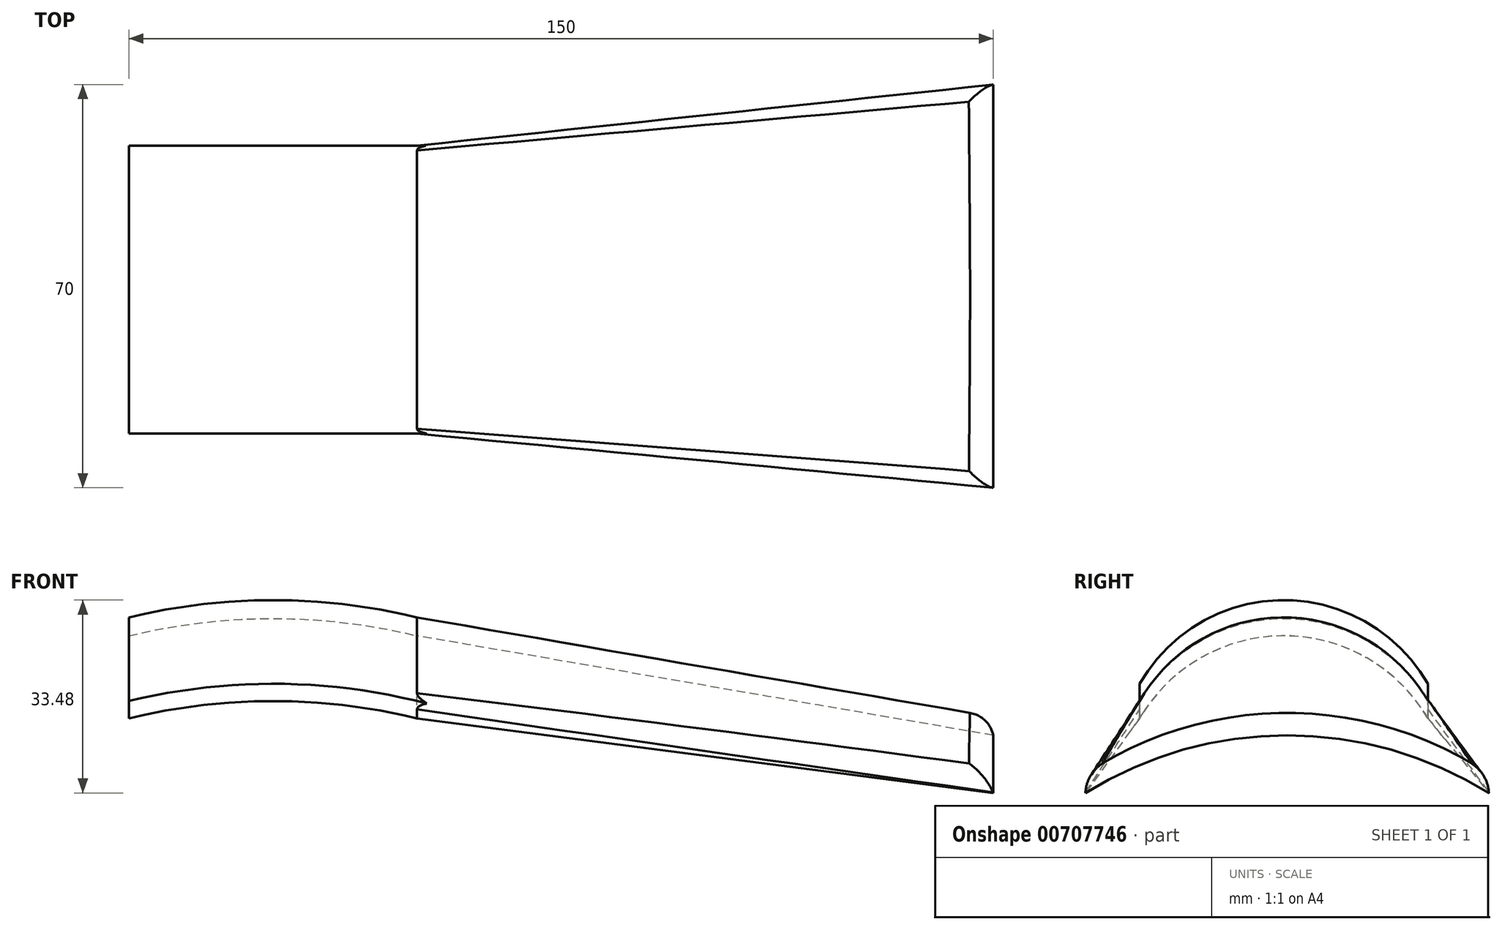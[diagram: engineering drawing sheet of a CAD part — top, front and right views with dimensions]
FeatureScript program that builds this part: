
annotation { "Feature Type Name" : "Feature", "Feature Type Description" : "" }
export const myFeature = defineFeature(function(context is Context, id is Id, definition is map)
    precondition{}
    {
        {
            var Q0;
            Q0=qCreatedBy(makeId("Right.planeOp"),FACE);
            var sketch = newSketch(context, id + "F0", { "sketchPlane" : qUnion([Q0])});
            skArc(sketch, "E0", {"start": v(50, 0) * mm, "mid": v(25, 14.53) * mm, "end": v(0, 0) * mm});
            skArc(sketch, "E1", {"start": v(50, -3) * mm, "mid": v(25, 11.33) * mm, "end": v(0, -3) * mm});
            skLineSegment(sketch, "E2", {"start": v(0, 0) * mm, "end": v(0, -3) * mm});
            skLineSegment(sketch, "E3", {"start": v(50, 0) * mm, "end": v(50, -3) * mm});
            skSolve(sketch);
        }
        {
            var Q0;
            Q0=qCreatedBy(makeId("Front.planeOp"),FACE);
            var sketch = newSketch(context, id + "F1", { "sketchPlane" : qUnion([Q0])});
            skArc(sketch, "E4", {"start": v(0, 0) * mm, "mid": v(-25, 3) * mm, "end": v(-50, 0) * mm});
            skLineSegment(sketch, "E5", {"start": v(-50, 0) * mm, "end": v(0, 0) * mm});
            skSolve(sketch);
        }
        {
            var Q0;
            Q0=makeQuery(id+"F0.imprint","IMPRINT",FACE,{"disambiguationData":[TD([[makeQuery(id+"F0.imprint","IMPRINT",EDGE,{"derivedFrom":sQuery(id+"F0.wireOp",EDGE,"E0")}),1.0]])]});
            var Q1;
            Q1=sQuery(id+"F1.wireOp",EDGE,"E4");
            sweep(context, id + "F2", {"profiles" : qUnion([Q0]), "path" : qUnion([Q1]), "keepProfileOrientation" : true});
        }
        {
            var Q0;
            Q0=qCreatedBy(makeId("Right.planeOp"),FACE);
            cPlane(context, id + "F3", {"entities" : qUnion([Q0]), "cplaneType" : CPlaneType.OFFSET, "offset" : 100 * mm, "width" : 150 * mm, "height" : 150 * mm});
        }
        {
            var Q0;
            Q0=qCreatedBy(id+"F3.planeOp",FACE);
            var sketch = newSketch(context, id + "F4", { "sketchPlane" : qUnion([Q0])});
            skArc(sketch, "E6", {"start": v(60.6, -12.95) * mm, "mid": v(25.6, -2.76) * mm, "end": v(-9.4, -12.95) * mm});
            skArc(sketch, "E7", {"start": v(60.6, -15.95) * mm, "mid": v(25.6, -5.95) * mm, "end": v(-9.4, -15.95) * mm});
            skLineSegment(sketch, "E8", {"start": v(-9.4, -12.95) * mm, "end": v(-9.4, -15.95) * mm});
            skLineSegment(sketch, "E9", {"start": v(60.6, -12.95) * mm, "end": v(60.6, -15.95) * mm});
            skSolve(sketch);
        }
        {
            var Q1;
            Q1=makeQuery(id+"F0.imprint","IMPRINT",FACE,{"disambiguationData":[TD([[makeQuery(id+"F0.imprint","IMPRINT",EDGE,{"derivedFrom":sQuery(id+"F0.wireOp",EDGE,"E0")}),1.0]])]});
            var Q2;
            Q2=makeQuery(id+"F4.imprint","IMPRINT",FACE,{"disambiguationData":[TD([[makeQuery(id+"F4.imprint","IMPRINT",EDGE,{"derivedFrom":sQuery(id+"F4.wireOp",EDGE,"E6")}),1.0]])]});
            loft(context, id + "F5", {"operationType" : NewBodyOperationType.ADD, "sheetProfilesArray" : [{ "sheetProfileEntities" : qUnion([Q1]) }, { "sheetProfileEntities" : qUnion([Q2]) }]});
        }
        {
            var Q0;
            Q0=makeQuery(id+"F5.opLoft","SWEPT_EDGE",EDGE,{"disambiguationData":[OSD([sQuery(id+"F0.wireOp",EDGE,"E0"),sQuery(id+"F0.wireOp",EDGE,"E2"),sQuery(id+"F4.wireOp",EDGE,"E6"),sQuery(id+"F4.wireOp",EDGE,"E8")])]});
            var Q1;
            Q1=makeQuery(id+"F5.opLoft","MID_CAP_EDGE",EDGE,{"disambiguationData":[OSD([sQuery(id+"F4.wireOp",EDGE,"E6"),sQuery(id+"F4.wireOp",EDGE,"E8"),sQuery(id+"F4.wireOp",EDGE,"E9")])],"capPos":1.0});
            var Q2;
            Q2=makeQuery(id+"F5.opLoft","SWEPT_EDGE",EDGE,{"disambiguationData":[OSD([sQuery(id+"F0.wireOp",EDGE,"E0"),sQuery(id+"F0.wireOp",EDGE,"E3"),sQuery(id+"F4.wireOp",EDGE,"E6"),sQuery(id+"F4.wireOp",EDGE,"E9")])]});
            fillet(context, id + "F6", {"entities" : qUnion([Q0, Q1, Q2]), "radius" : 5 * mm, "tangentPropagation" : true, "allowEdgeOverflow" : false});
        }
    });
